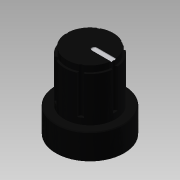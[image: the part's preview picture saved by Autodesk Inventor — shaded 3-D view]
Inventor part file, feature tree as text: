
AUTODESK INVENTOR PART (.ipt)
format: ipt  version: 2019 (Build 230136000, 136)  size: 397,824 bytes
history: native  units: mm
features: extrude x5, sketch x3, hole x1, pattern_circular x1, fillet x1, chamfer x1
ambient origin geometry x8: Origin, YZ Plane, XZ Plane, XY Plane, X Axis, Y Axis, Z Axis, Center Point
bodies: Solid1 (feature_tree)
feature tree (12):
  sketch  "Sketch1"  dims[d0=19.0mm d1=14.2mm]
  extrude  "Extrusion1"  Depth=14.2mm
  extrude  "Extrusion2"  Depth=7.0mm TaperAngle=0.0deg
  hole  "Hole1"  [1 undecoded]
  sketch  "Sketch2"  dims[d2=14.0mm d3=0.0mm d4=7.0mm d5=0.0mm]
  extrude  "Extrusion3"  Depth=0.25mm TaperAngle=360.0deg
  pattern_circular  "Circular Pattern1"  [2 undecoded]
  extrude  "Extrusion4"  Depth=0.25mm TaperAngle=0.0deg
  extrude  "Extrusion5"  Depth=0.25mm
  fillet  "Fillet1"  Radius=0.7mm
  chamfer  "Chamfer1"  Distance=0.7mm
  sketch  "Sketch3"  dims[d6=10.0mm d7=10.0mm d8=6.0mm d9=6.0mm d10=4.0mm d11=2.0mm d12=90.0deg d13=10.0mm d14=0.0mm d15=12.3mm d16=0.0mm d17=60.0mm d18=360.0deg d20=1.65mm d21=0.0mm d22=0.25mm d23=0.0mm d24=0.25mm d25=0.7mm d26=0.7mm d27=0.2mm d28=2.0mm d29=45.0deg]
note: 3 required parameter values undecoded (feature->parameter linkage not recoverable at this tier; creation-order binding heuristic only, values carry confidence <= 0.55)
